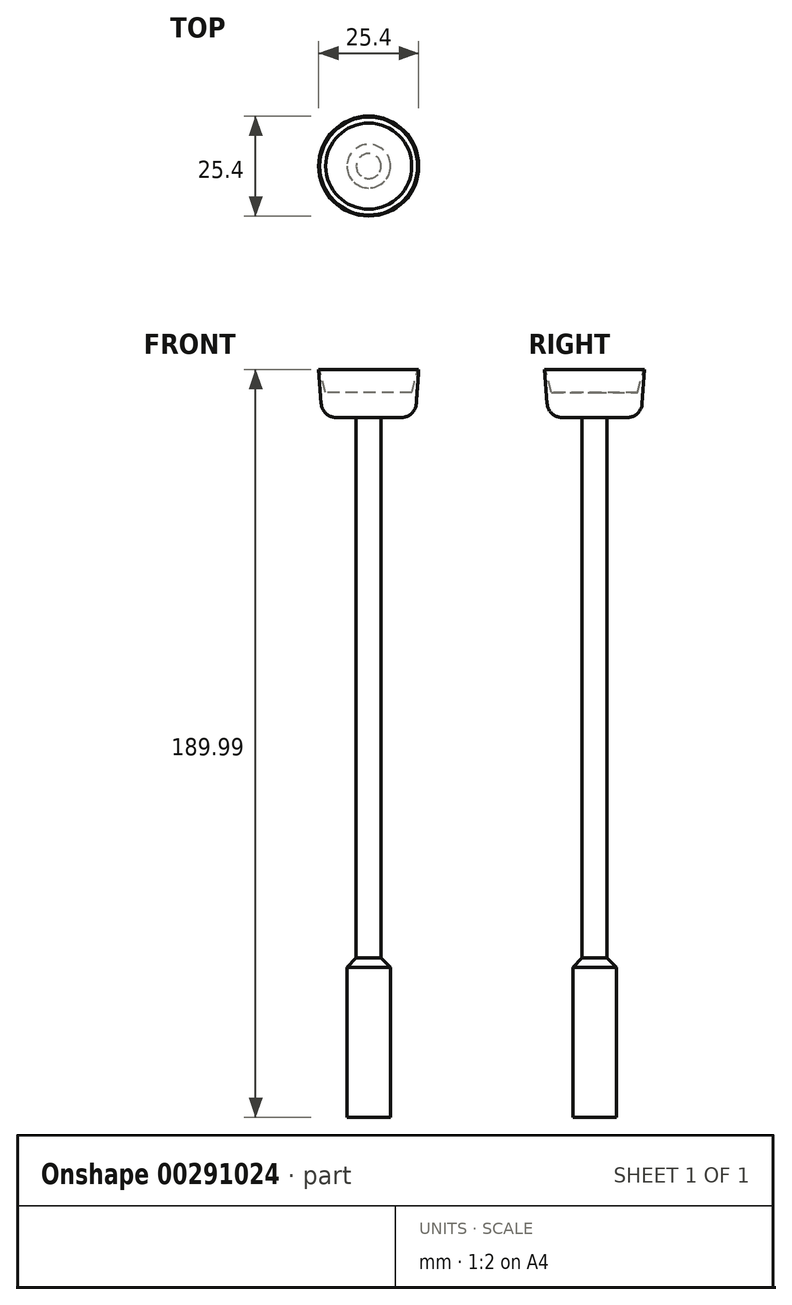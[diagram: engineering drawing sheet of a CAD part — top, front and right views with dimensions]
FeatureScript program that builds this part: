
annotation { "Feature Type Name" : "Feature", "Feature Type Description" : "" }
export const myFeature = defineFeature(function(context is Context, id is Id, definition is map)
    precondition{}
    {
        {
            var Q0;
            Q0=qCreatedBy(makeId("Front.planeOp"),FACE);
            var sketch = newSketch(context, id + "F0", { "sketchPlane" : qUnion([Q0])});
            skLineSegment(sketch, "E0", {"start": v(0, 0) * mm, "end": v(11.81, 0) * mm});
            skLineSegment(sketch, "E1", {"start": v(11.81, 0) * mm, "end": v(12.7, 12.2) * mm});
            skLineSegment(sketch, "E2", {"start": v(10.92, 6.35) * mm, "end": v(0, 6.35) * mm});
            skLineSegment(sketch, "E3", {"start": v(0, 6.35) * mm, "end": v(0, 0) * mm});
            skLineSegment(sketch, "E4", {"start": v(12.7, 12.2) * mm, "end": v(12.45, 12.2) * mm});
            skLineSegment(sketch, "E5", {"start": v(12.45, 12.2) * mm, "end": v(10.92, 6.35) * mm});
            skSolve(sketch);
        }
        {
            var Q0;
            Q0=makeQuery(id+"F0.imprint","IMPRINT",FACE,{"disambiguationData":[TD([[makeQuery(id+"F0.imprint","IMPRINT",EDGE,{"derivedFrom":sQuery(id+"F0.wireOp",EDGE,"E0")}),1.0]])]});
            var Q1;
            Q1=sQuery(id+"F0.wireOp",EDGE,"E3");
            revolve(context, id + "F1", {"entities" : qUnion([Q0]), "axis" : qUnion([Q1]), "revolveType" : RevolveType.FULL});
        }
        {
            var Q0;
            Q0=makeQuery(id+"F1.opRevolve","SWEPT_EDGE",EDGE,{"disambiguationData":[OSD([sQuery(id+"F0.wireOp",EDGE,"E0"),sQuery(id+"F0.wireOp",EDGE,"E1")])]});
            fillet(context, id + "F2", {"entities" : qUnion([Q0]), "radius" : 3.8 * mm, "tangentPropagation" : true, "allowEdgeOverflow" : false});
        }
        {
            var Q0;
            Q0=makeQuery(id+"F1.opRevolve","SWEPT_FACE",FACE,{"disambiguationData":[OSD([sQuery(id+"F0.wireOp",EDGE,"E0")])]});
            var sketch = newSketch(context, id + "F3", { "sketchPlane" : qUnion([Q0])});
            skCircle(sketch, "E6", {"center": v(0, 0) * mm, "radius": 3.18 * mm});
            skSolve(sketch);
        }
        {
            var Q0;
            Q0=qSketchRegion(id+"F3",true);
            extrude(context, id + "F4", {"entities" : qUnion([Q0]), "operationType" : NewBodyOperationType.ADD, "depth" : 139.7 * mm});
        }
        {
            var Q0;
            Q0=makeQuery(id+"F4.opExtrude","CAP_FACE",FACE,{"disambiguationData":[OSD([sQuery(id+"F3.wireOp",EDGE,"E6")])],"isStart":false});
            var sketch = newSketch(context, id + "F5", { "sketchPlane" : qUnion([Q0])});
            skCircle(sketch, "E7", {"center": v(0, 0) * mm, "radius": 5.54 * mm});
            skSolve(sketch);
        }
        {
            var Q0;
            Q0 = qSketchRegion(id + "F5", true);
            extrude(context, id + "F6", {"entities" : qUnion([Q0]), "operationType" : NewBodyOperationType.ADD, "depth" : 38.1 * mm});
        }
        {
            var Q0;
            Q0=qCreatedBy(makeId("Front.planeOp"),FACE);
            var sketch = newSketch(context, id + "F7", { "sketchPlane" : qUnion([Q0])});
            skLineSegment(sketch, "E8", {"start": v(0, -139.7) * mm, "end": v(-5.54, -139.7) * mm});
            skLineSegment(sketch, "E9", {"start": v(-5.54, -139.7) * mm, "end": v(0, -134.16) * mm});
            skLineSegment(sketch, "E10", {"start": v(0, -134.16) * mm, "end": v(0, -139.7) * mm});
            skSolve(sketch);
        }
        {
            var Q0;
            Q0=makeQuery(id+"F7.imprint","IMPRINT",FACE,{"disambiguationData":[TD([[makeQuery(id+"F7.imprint","IMPRINT",EDGE,{"derivedFrom":sQuery(id+"F7.wireOp",EDGE,"E8")}),-1.0]])]});
            var Q1;
            Q1=sQuery(id+"F7.wireOp",EDGE,"E10");
            revolve(context, id + "F8", {"operationType" : NewBodyOperationType.ADD, "entities" : qUnion([Q0]), "axis" : qUnion([Q1]), "revolveType" : RevolveType.FULL});
        }
    });
